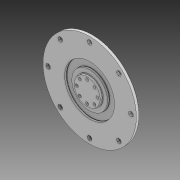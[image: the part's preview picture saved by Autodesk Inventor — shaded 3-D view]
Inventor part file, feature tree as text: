
AUTODESK INVENTOR PART (.ipt)
format: ipt  version: 2020 (Build 240168000, 168)  size: 367,104 bytes
history: native  units: mm
features: sketch x8, extrude x5, revolve x1, chamfer x1
ambient origin geometry x8: Origin, YZ Plane, XZ Plane, XY Plane, X Axis, Y Axis, Z Axis, Center Point
bodies: Solid1 (feature_tree)
feature tree (15):
  extrude  "Extrusion1"  Depth=2.0mm TaperAngle=0.0deg
  sketch  "Sketch2"  dims[d3=400.0mm d4=600.0mm]
  revolve  "Revolution1"  [1 undecoded]
  extrude  "Extrusion2"  Depth=1000.0mm
  extrude  "Extrusion3"  TaperAngle=90.0deg  [1 undecoded]
  extrude  "Extrusion4"  Depth=20.0mm
  extrude  "Extrusion5"  TaperAngle=0.0deg  [1 undecoded]
  chamfer  "Chamfer1"  Distance=80.0mm Angle=360.0deg
  sketch  "Sketch8"  dims[d29=6.0mm d30=0.0mm d33=25.0mm d36=1.5mm d38=5.0mm d39=4.0mm d40=8.7mm d41=4.0mm d43=0.8mm d44=34.9mm d45=47.6mm d46=80.0mm d47=5.5mm d48=80.0mm d50=360.0deg d52=0.0mm d53=0.0mm d54=8.2mm d55=80.0mm d57=360.0deg d59=4.0mm d60=0.0mm d61=1.0mm d62=2.0mm d63=45.0deg d64=0.5mm d66=0.5mm]
  sketch  "Sketch1"  dims[d0=180.0mm d1=2.0mm d2=0.0mm]
  sketch  "Sketch3"  dims[d5=800.0mm d6=1000.0mm]
  sketch  "Sketch4"  dims[d9=0.0mm d14=90.0deg]
  sketch  "Sketch5"  dims[d16=20.0mm d17=5.5mm]
  sketch  "Sketch6"  dims[d18=80.0mm d20=360.0deg d22=0.0mm d23=0.0mm]
  sketch  "Sketch7"  dims[d24=9.5mm d25=80.0mm d27=360.0deg]
note: 3 required parameter values undecoded (feature->parameter linkage not recoverable at this tier; creation-order binding heuristic only, values carry confidence <= 0.55)